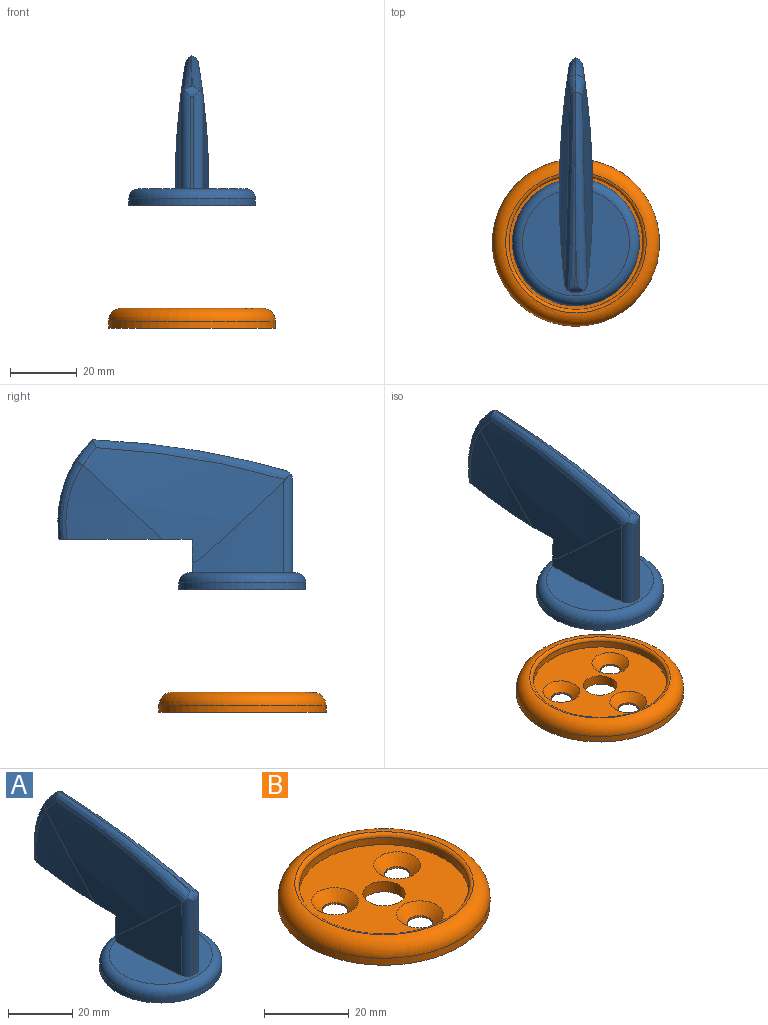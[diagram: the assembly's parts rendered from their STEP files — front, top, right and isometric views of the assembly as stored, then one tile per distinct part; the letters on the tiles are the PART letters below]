
ASSEMBLY  parts=2 mates=1
PART A: 30 faces, bbox 41.2x80.1x47.3 mm
  f0: plane 39.98x9.79mm, normal (0,0,-1), area 306.9mm2, adj f2,f4,f15,f16,f19,f26,f28
  f1: plane 27.74x0.93mm, normal (0,-1,0), area 25.8mm2, adj f6,f20,f22,f23
  f2: cylinder r=213.42mm len=60.44mm, axis (0,1,0), area 1054.3mm2, adj f0,f4,f16,f17,f20,f21,f24
  f3: cylinder r=252.75mm len=10.53mm, axis (-1,0,0), area 3.9mm2, adj f21,f22,f25
  f4: plane 10x10mm, normal (0,1,0), area 70.8mm2, adj f0,f2,f6,f14,f15,f17,f18
  f5: plane 6x5mm, normal (0,-1,0), area 15.9mm2, adj f8,f11,f13,f14
  f6: plane 32x32mm, normal (0,0,1), area 544.6mm2, adj f1,f4,f17,f18,f20,f23,f29
  f7: plane 15x6mm, normal (0,1,0), area 90mm2, adj f8,f11,f12,f13
  f8: plane 15x6mm, normal (1,0,0), area 90mm2, adj f5,f7,f9,f12,f13
  f9: plane 10x6mm, normal (0,-1,0), area 45.9mm2, adj f8,f11,f12,f14
  f10: cylinder r=19mm len=38mm, axis (0,0,1), area 238.8mm2, adj f12,f29
  f11: plane 15x6mm, normal (-1,0,0), area 90mm2, adj f5,f7,f9,f12,f13
  f12: plane 38x38mm, normal (0,0,-1), area 1098.1mm2, adj f7,f8,f9,f10,f11
  f13: plane 6x6mm, normal (0,0,-1), area 36mm2, adj f5,f7,f8,f11
  f14: cylinder r=3mm len=12mm, axis (0,1,0), area 226.2mm2, adj f4,f5,f9
  f15: cylinder r=213.42mm len=60.44mm, axis (0,1,0), area 1054.3mm2, adj f0,f4,f18,f19,f23,f25,f27
  f16: cylinder r=241.62mm len=28.87mm, axis (0,0,1), area 351mm2, adj f0,f2,f24,f26
  f17: cylinder r=241.62mm len=27.34mm, axis (0,0,1), area 413.6mm2, adj f2,f4,f6,f20
  f18: cylinder r=241.62mm len=27.34mm, axis (0,0,1), area 413.6mm2, adj f4,f6,f15,f23
  f19: cylinder r=241.62mm len=28.87mm, axis (0,0,1), area 351mm2, adj f0,f15,f27,f28
  f20: cylinder r=3mm len=29.53mm, axis (0,0,1), area 124.9mm2, adj f1,f2,f6,f17,f21,f22
  f21: bspline ~79.67x15.81mm, area 227.4mm2, adj f2,f3,f20,f22,f24,f25
  f22: cylinder r=3mm len=4.5mm, axis (-1,0,0), area 10.3mm2, adj f1,f3,f20,f21,f23,f25
  f23: cylinder r=3mm len=29.53mm, axis (0,0,1), area 124.9mm2, adj f1,f6,f15,f18,f22,f25
  f24: bspline ~12.08x10.56mm, area 28mm2, adj f2,f16,f21,f26,f27
  f25: bspline ~79.67x15.81mm, area 227.4mm2, adj f3,f15,f21,f22,f23,f27
  f26: bspline ~30x9.09mm, area 89.6mm2, adj f0,f16,f24,f28
  f27: bspline ~12.08x10.56mm, area 28mm2, adj f15,f19,f24,f25,f28
  f28: bspline ~30x9.09mm, area 89.6mm2, adj f0,f19,f26,f27
  f29: torus R=16mm, axis (0,0,1), area 530.3mm2, adj f6,f10
PART B: 13 faces, bbox 54.1x54.1x6 mm
  f0: cylinder r=3.02mm len=6.04mm, axis (0,0,1), area 9.5mm2, adj f5,f10
  f1: cylinder r=3.02mm len=6.04mm, axis (0,0,1), area 9.5mm2, adj f5,f9
  f2: cylinder r=4.99mm len=9.99mm, axis (0,0,1), area 94.1mm2, adj f5,f7
  f3: cylinder r=3.02mm len=6.04mm, axis (0,0,1), area 9.5mm2, adj f5,f8
  f4: cylinder r=25mm len=50mm, axis (0,0,1), area 314.2mm2, adj f5,f11
  f5: plane 50x50mm, normal (0,0,-1), area 1799.2mm2, adj f0,f1,f2,f3,f4
  f6: cylinder r=20.02mm len=40.04mm, axis (0,0,1), area 251.6mm2, adj f7,f12
  f7: plane 40.04x40.04mm, normal (0,0,1), area 893.8mm2, adj f2,f6,f8,f9,f10
  f8: cone r=3.02mm half-angle=45deg, axis (0,0,1), area 94.9mm2, adj f3,f7
  f9: cone r=3.02mm half-angle=45deg, axis (0,0,1), area 94.9mm2, adj f1,f7
  f10: cone r=3.02mm half-angle=45deg, axis (0,0,1), area 94.9mm2, adj f0,f7
  f11: torus R=21mm, axis (0,0,1), area 925.8mm2, adj f4,f12
  f12: torus R=21.02mm, axis (0,0,-1), area 202.1mm2, adj f6,f11
PLACE A t=(-28.45,-18.86,40.65)mm
PLACE B t=(-34.49,-20.85,4.95)mm
MATE parallel B.f2 <-> A.f10  axis (0,0,1) through (-28.45,-18.86,1.95)mm
